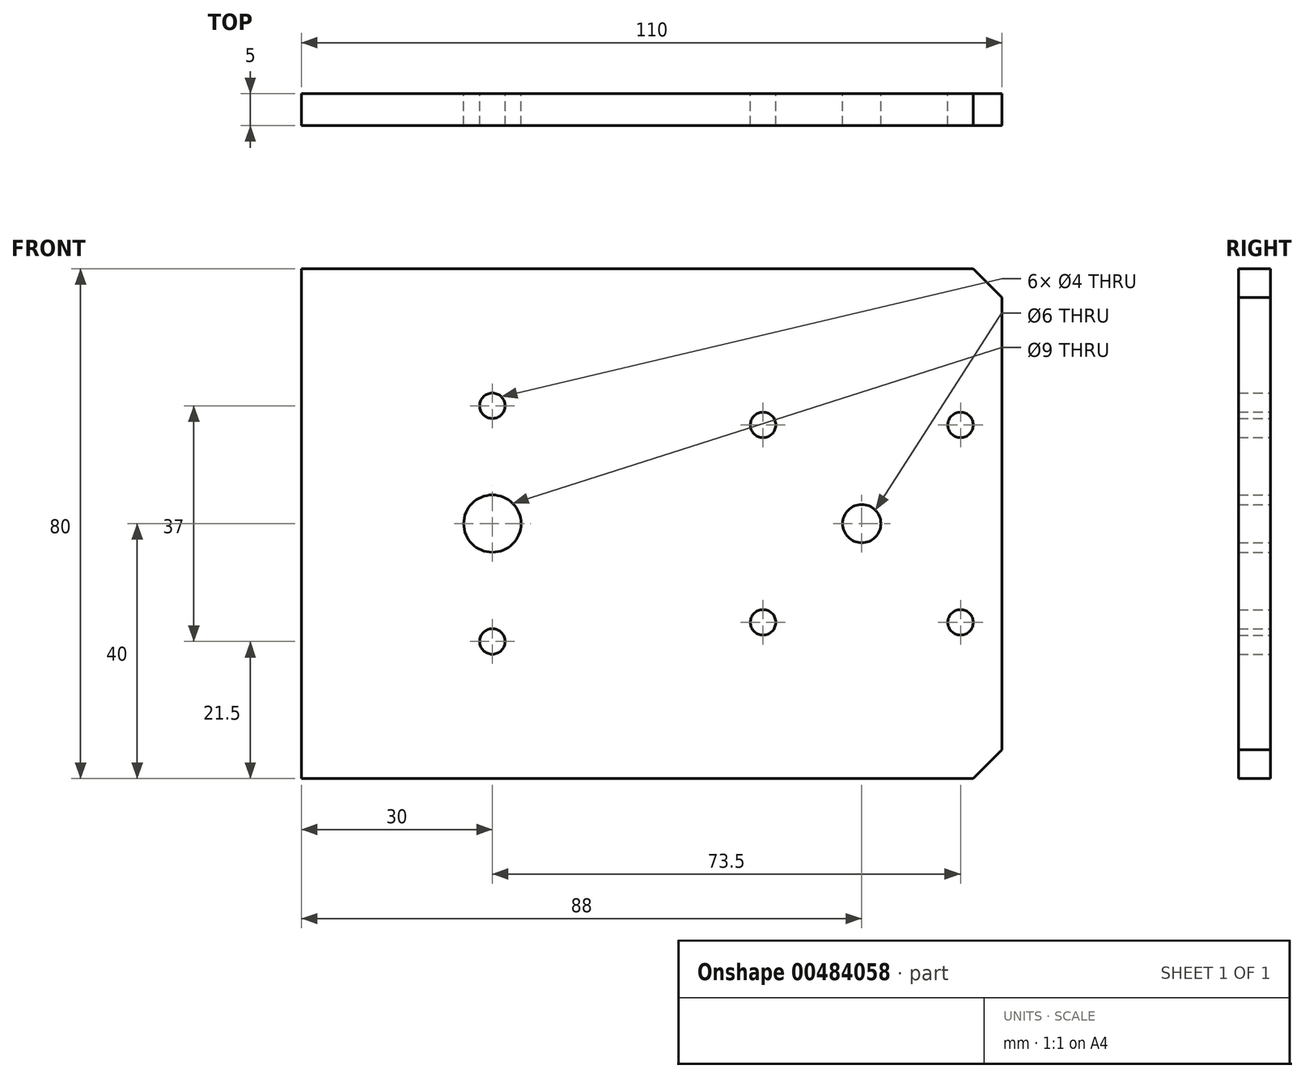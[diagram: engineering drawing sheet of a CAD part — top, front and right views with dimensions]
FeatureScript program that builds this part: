
annotation { "Feature Type Name" : "Feature", "Feature Type Description" : "" }
export const myFeature = defineFeature(function(context is Context, id is Id, definition is map)
    precondition{}
    {
        {
            var Q0;
            Q0=qCreatedBy(makeId("Front.planeOp"),FACE);
            var sketch = newSketch(context, id + "F0", { "sketchPlane" : qUnion([Q0])});
            skLineSegment(sketch, "E0.bottom", {"start": v(55, 40) * mm, "end": v(-55, 40) * mm});
            skLineSegment(sketch, "E0.top", {"start": v(55, -40) * mm, "end": v(-55, -40) * mm});
            skLineSegment(sketch, "E0.left", {"start": v(55, 40) * mm, "end": v(55, -40) * mm});
            skLineSegment(sketch, "E0.right", {"start": v(-55, 40) * mm, "end": v(-55, -40) * mm});
            skPoint(sketch, "E0.middle", {"position": v(0, 0) * mm});
            skCircle(sketch, "E1", {"center": v(-25, 0) * mm, "radius": 4.5 * mm});
            skCircle(sketch, "E2", {"center": v(33, 0) * mm, "radius": 3 * mm});
            skCircle(sketch, "E3", {"center": v(17.5, 15.5) * mm, "radius": 2 * mm});
            skCircle(sketch, "E4", {"center": v(48.5, 15.5) * mm, "radius": 2 * mm});
            skCircle(sketch, "E5", {"center": v(48.5, -15.5) * mm, "radius": 2 * mm});
            skCircle(sketch, "E6", {"center": v(17.5, -15.5) * mm, "radius": 2 * mm});
            skCircle(sketch, "E7", {"center": v(-25, 18.5) * mm, "radius": 2 * mm});
            skCircle(sketch, "E8", {"center": v(-25, -18.5) * mm, "radius": 2 * mm});
            skSolve(sketch);
        }
        {
            var Q0;
            Q0 = qSketchRegion(id + "F0", true);
            extrude(context, id + "F1", {"entities" : qUnion([Q0]), "depth" : 5 * mm});
        }
        {
            var Q0;
            Q0=makeQuery(id+"F1.opExtrude","SWEPT_EDGE",EDGE,{"disambiguationData":[OSD([sQuery(id+"F0.wireOp",EDGE,"E0.bottom"),sQuery(id+"F0.wireOp",EDGE,"E0.left")])]});
            chamfer(context, id + "F2", {"entities" : qUnion([Q0]), "width" : 4.5 * mm, "tangentPropagation" : true});
        }
        {
            var Q0;
            Q0=makeQuery(id+"F1.opExtrude","SWEPT_EDGE",EDGE,{"disambiguationData":[OSD([sQuery(id+"F0.wireOp",EDGE,"E0.top"),sQuery(id+"F0.wireOp",EDGE,"E0.left")])]});
            chamfer(context, id + "F3", {"entities" : qUnion([Q0]), "width" : 4.5 * mm, "tangentPropagation" : true});
        }
    });
